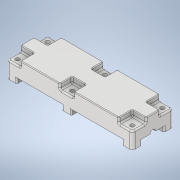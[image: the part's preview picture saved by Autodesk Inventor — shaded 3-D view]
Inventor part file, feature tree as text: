
AUTODESK INVENTOR PART (.ipt)
format: ipt  version: 2021 (Build 250183000, 183)  size: 887,808 bytes
history: native  units: mm
features: sketch x23, extrude x22, projected_geometry x9, fillet x3, other x1, mirror x1, boolean_combine x1
ambient origin geometry x8: Origin, YZ Plane, XZ Plane, XY Plane, X Axis, Y Axis, Z Axis, Center Point
bodies: Volumenkörper1 (feature_tree), Solid2 (feature_tree), Solid3 (feature_tree)
feature tree (60):
  extrude  "Extrusion1"  Depth=11.0mm
  other  "Spirale1"
  mirror  "Spiegeln1"
  extrude  "Extrusion5"  Depth=4.0mm
  extrude  "Extrusion6"  Depth=1.0mm
  boolean_combine  "Combine1"
  extrude  "Extrusion7"  Depth=10.0mm TaperAngle=0.0deg
  extrude  "Extrusion8"  Depth=7.0mm TaperAngle=0.0deg
  extrude  "Extrusion9"  Depth=24.0mm
  extrude  "Extrusion10"  Depth=12.0mm TaperAngle=0.0deg
  extrude  "Extrusion11"  Depth=4.0mm
  extrude  "Extrusion13"  Depth=10.0mm
  fillet  "Fillet2"  Radius=10.0mm
  fillet  "Fillet3"  Radius=77.15mm
  fillet  "Fillet4"  Radius=30.0mm
  extrude  "Extrusion14"  Depth=4.0mm
  extrude  "Extrusion15"  Depth=10.0mm TaperAngle=0.0deg
  extrude  "Extrusion16"  Depth=3.0mm
  extrude  "Extrusion17"  Depth=4.0mm
  extrude  "Extrusion19"  Depth=4.0mm
  extrude  "Extrusion20"  Depth=6.9mm
  extrude  "Extrusion21"  Depth=7.0mm
  extrude  "Extrusion22"  Depth=6.9mm
  extrude  "Extrusion23"  Depth=10.0mm
  extrude  "Extrusion25"  Depth=10.0mm
  extrude  "Extrusion26"  Depth=10.0mm
  extrude  "Extrusion27"  Depth=10.0mm
  extrude  "Extrusion28"  Depth=10.0mm
  sketch  "Skizze1"  dims[d0=6.0mm d1=11.0mm]
  sketch  "Skizze3"  dims[d2=36.0mm d3=0.0mm]
  projected_geometry  "Projizierte Kontur2"
  sketch  "Sketch7"  dims[d8=7.0mm d9=24.5mm d10=10.0mm d11=0.0mm d12=90.0deg d13=90.0deg d14=0.0mm d15=0.0mm d16=4.0mm]
  sketch  "Sketch8"  dims[d17=13.962634mm d18=1.0mm]
  sketch  "Sketch9"  dims[d19=0.1mm d32=10.0mm d33=0.0mm]
  projected_geometry  "Projected Loop4"
  sketch  "Sketch10"  dims[d34=7.0mm d35=100.0mm d36=0.0mm]
  sketch  "Sketch11"  dims[d37=82.0mm d38=0.0mm d39=24.0mm]
  projected_geometry  "Projected Loop5"
  projected_geometry  "Projected Loop6"
  sketch  "Sketch12"  dims[d40=30.0mm d41=12.0mm d42=0.0mm]
  sketch  "Sketch13"  dims[d43=3.0mm d44=4.0mm]
  projected_geometry  "Projected Loop7"
  projected_geometry  "Projected Loop8"
  sketch  "Sketch15"  dims[d45=4.0mm d46=20.0mm d48=22.0mm d49=20.0mm d51=84.0mm d54=10.0mm d55=0.0mm d56=77.15mm d57=30.0mm]
  sketch  "Sketch16"  dims[d62=4.0mm d63=0.0mm d64=6.0mm]
  projected_geometry  "Projected Loop10"
  sketch  "Sketch17"  dims[d65=10.0mm d66=0.0mm d67=10.0mm d68=0.0mm]
  projected_geometry  "Projected Loop11"
  projected_geometry  "Projected Loop12"
  sketch  "Sketch18"  dims[d76=3.0mm d77=3.0mm]
  sketch  "Sketch19"  dims[d78=4.0mm d79=48.0mm]
  sketch  "Sketch21"  dims[d80=46.0mm d81=4.0mm]
  sketch  "Sketch22"  dims[d85=7.0mm d86=6.9mm]
  sketch  "Sketch23"  dims[d87=3.5mm d88=7.0mm]
  sketch  "Sketch24"  dims[d89=6.9mm d90=3.5mm]
  sketch  "Sketch25"  dims[d91=10.0mm d92=10.0mm]
  sketch  "Sketch27"  dims[d93=10.0mm d94=10.0mm]
  sketch  "Sketch28"  dims[d95=10.0mm d96=10.0mm]
  sketch  "Sketch29"  dims[d97=10.0mm d98=10.0mm]
  sketch  "Sketch30"  dims[d99=10.0mm d100=10.0mm d101=10.0mm d102=10.0mm d103=4.0mm d104=0.0mm d105=1.0mm d106=1.0mm d107=2.0mm d108=0.5mm d109=6.5mm d110=2.1mm d111=0.0mm d112=6.5mm d113=2.1mm d114=0.0mm d115=180.0deg d116=6.9mm d117=6.9mm d118=6.9mm d119=6.9mm d120=12.0mm d121=0.2mm d122=0.0mm d123=15.0mm d124=0.2mm d125=0.0mm d126=7.9mm d127=0.0mm d128=7.9mm d129=0.0mm d132=1.9mm d133=0.0mm d134=5.1mm d135=5.0mm d136=0.0mm d137=6.6mm d138=1.9mm d139=0.0mm d140=4.1mm d141=3.1mm d142=0.0mm d143=6.6mm d144=3.1mm d145=0.0mm d149=6.6mm d150=0.2mm d151=0.0mm d152=5.1mm d153=7.9mm d154=0.0mm d155=2.0mm d156=0.0mm d157=5.1mm d158=5.1mm d159=1.0mm d160=2.0mm d161=0.0mm d162=0.5mm d163=0.872665mm]
